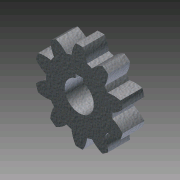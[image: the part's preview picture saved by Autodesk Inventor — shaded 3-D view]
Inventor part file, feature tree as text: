
AUTODESK INVENTOR PART (.ipt)
format: ipt  version: 2011 (Build 150239000, 239)  size: 201,728 bytes
history: native  units: mm (DEFAULTED — no unit token found)
features: sketch x4, extrude x3, plane x3, other x3
ambient origin geometry x8: Origin, YZ Plane, XZ Plane, XY Plane, X Axis, Y Axis, Z Axis, Center Point
bodies: Solid1 (feature_tree)
feature tree (13):
  extrude  "Extrusion1"  Depth=9.525mm TaperAngle=0.0deg
  plane  "Work Plane1"
  plane  "Work Plane2"
  plane  "Work Plane3"
  other  "Spur Gear"
  extrude  "Extrusion2"  Depth=76.2mm TaperAngle=0.0deg
  extrude  "Extrusion3"  TaperAngle=0.0deg  [1 undecoded]
  sketch  "Sketch1"  dims[d0=38.847059mm d1=9.525mm d2=0.0mm]
  sketch  "Sketch2"  dims[d3=30.97561mm d4=76.2mm d5=0.0mm]
  other  "Srf1"
  sketch  "Sketch3"  dims[d6=0.0mm d7=3.141593mm d9=0.0mm]
  sketch  "Sketch4"  dims[d14=0.0mm d15=63.5mm d16=0.0mm d17=0.0mm d18=0.0mm d19=63.5mm d20=12.7mm d21=25.4mm d22=0.0mm d23=3.175mm d24=1.5875mm d25=7.747mm d26=25.4mm d27=0.0mm]
  other  "Pitch Diameter"
note: 1 required parameter value undecoded (feature->parameter linkage not recoverable at this tier; creation-order binding heuristic only, values carry confidence <= 0.55)
